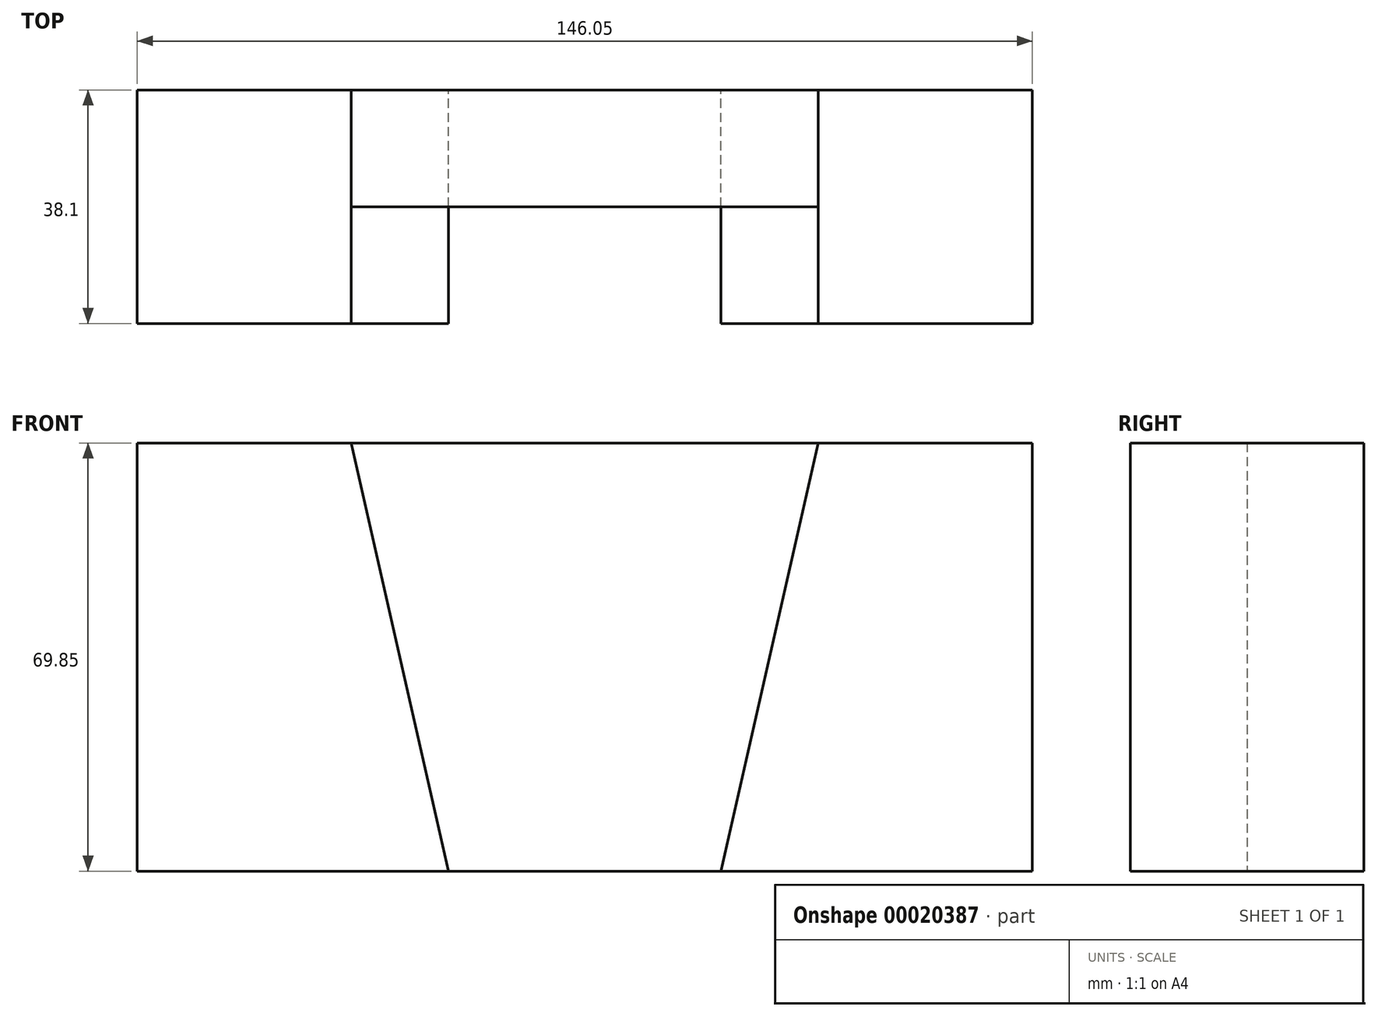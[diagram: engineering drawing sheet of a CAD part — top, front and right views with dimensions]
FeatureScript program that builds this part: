
annotation { "Feature Type Name" : "Feature", "Feature Type Description" : "" }
export const myFeature = defineFeature(function(context is Context, id is Id, definition is map)
    precondition{}
    {
        {
            var Q0;
            Q0=qCreatedBy(makeId("Front.planeOp"),FACE);
            var sketch = newSketch(context, id + "F0", { "sketchPlane" : qUnion([Q0])});
            skLineSegment(sketch, "E0.bottom", {"start": v(68.49, -26.98) * mm, "end": v(-77.56, -26.98) * mm});
            skLineSegment(sketch, "E0.top", {"start": v(68.49, 42.87) * mm, "end": v(-77.56, 42.87) * mm});
            skLineSegment(sketch, "E0.left", {"start": v(68.49, -26.98) * mm, "end": v(68.49, 42.87) * mm});
            skLineSegment(sketch, "E0.right", {"start": v(-77.56, -26.98) * mm, "end": v(-77.56, 42.87) * mm});
            skLineSegment(sketch, "E1", {"start": v(33.56, 42.87) * mm, "end": v(17.69, -26.98) * mm});
            skLineSegment(sketch, "E2", {"start": v(17.69, -26.98) * mm, "end": v(68.49, -26.98) * mm});
            skLineSegment(sketch, "E3", {"start": v(-42.64, 42.87) * mm, "end": v(-26.76, -26.98) * mm});
            skPoint(sketch, "E4.end.orphan", {"position": v(33.56, 105.9) * mm});
            skPoint(sketch, "E5.end.orphan", {"position": v(68.49, 105.9) * mm});
            skPoint(sketch, "E6.start.orphan", {"position": v(-42.64, 105.9) * mm});
            skPoint(sketch, "E7.end.orphan", {"position": v(68.49, -76.2) * mm});
            skPoint(sketch, "E8.end.orphan", {"position": v(17.69, -76.2) * mm});
            skSolve(sketch);
        }
        {
            var Q0;
            {var subQ1=sQuery(id+"F0.wireOp",EDGE,"E0.right");Q0=makeQuery(id+"F0.imprint","IMPRINT",FACE,{"disambiguationData":[TD([[makeQuery(id+"F0.imprint","IMPRINT",EDGE,{"derivedFrom":subQ1}),-1.0]])]});}
            var Q1;
            {var subQ1=sQuery(id+"F0.wireOp",EDGE,"E0.left");Q1=makeQuery(id+"F0.imprint","IMPRINT",FACE,{"disambiguationData":[TD([[makeQuery(id+"F0.imprint","IMPRINT",EDGE,{"derivedFrom":subQ1}),1.0]])]});}
            extrude(context, id + "F1", {"entities" : qUnion([Q0, Q1]), "depth" : 38.1 * mm});
        }
        {
            var Q0;
            {var subQ2=sQuery(id+"F0.wireOp",EDGE,"E1");Q0=makeQuery(id+"F0.imprint","IMPRINT",FACE,{"disambiguationData":[TD([[makeQuery(id+"F0.imprint","IMPRINT",EDGE,{"derivedFrom":subQ2}),-1.0]])]});}
            extrude(context, id + "F2", {"entities" : qUnion([Q0]), "depth" : 19.05 * mm});
        }
    });
